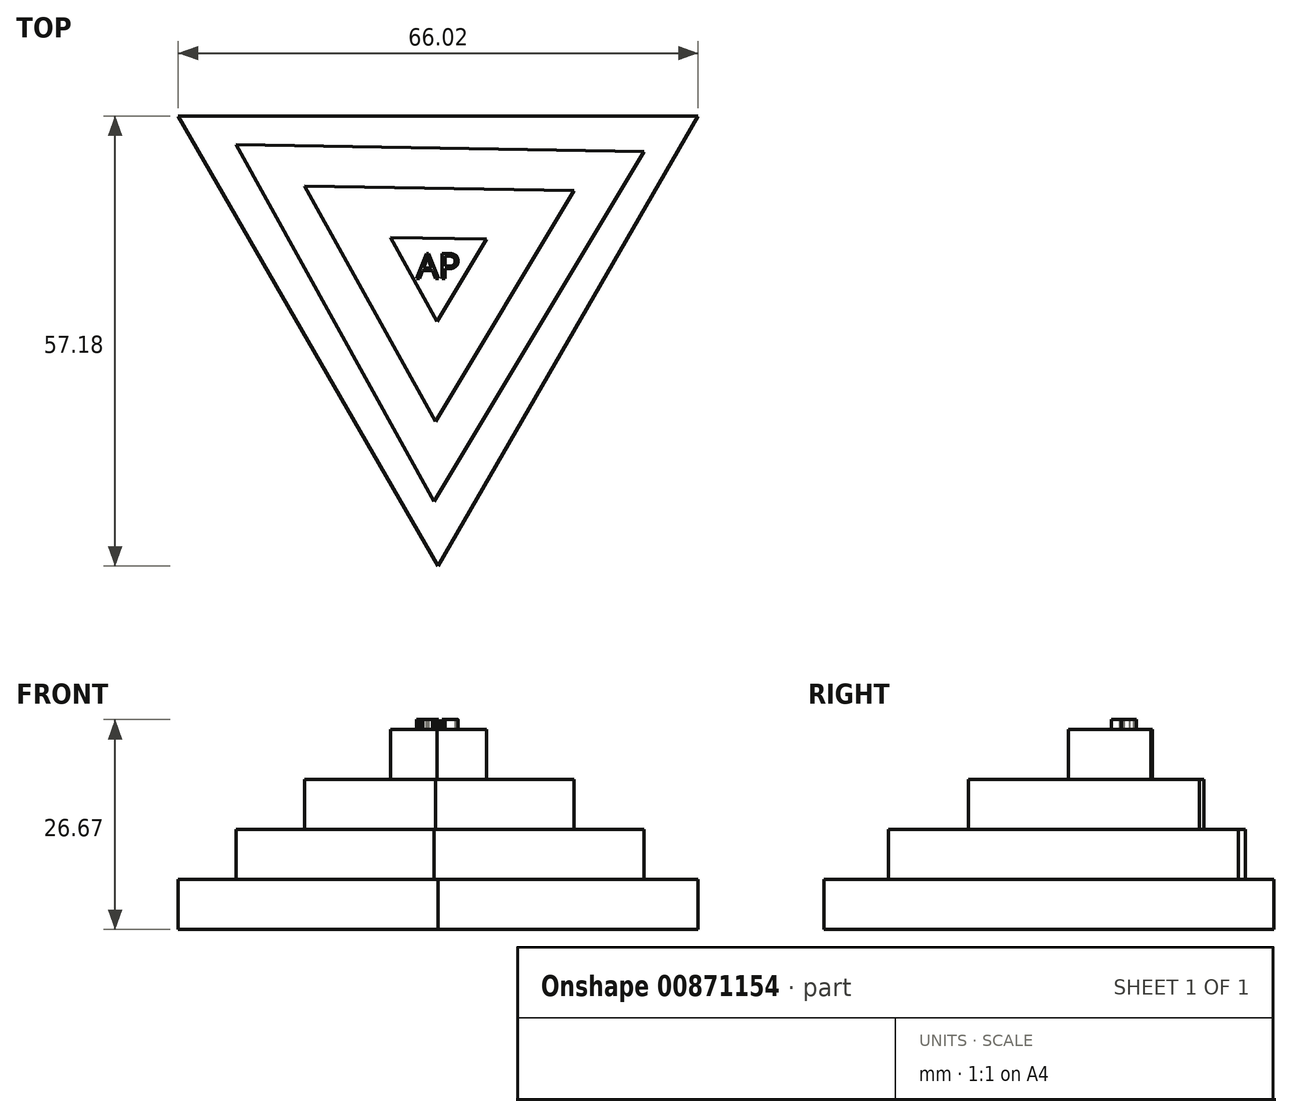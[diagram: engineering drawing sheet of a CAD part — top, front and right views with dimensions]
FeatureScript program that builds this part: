
annotation { "Feature Type Name" : "Feature", "Feature Type Description" : "" }
export const myFeature = defineFeature(function(context is Context, id is Id, definition is map)
    precondition{}
    {
        {
            var Q0;
            Q0=qCreatedBy(makeId("Top.planeOp"),FACE);
            var sketch = newSketch(context, id + "F0", { "sketchPlane" : qUnion([Q0])});
            skCircle(sketch, "E0.cCircle", {"center": v(0, 0) * mm, "radius": 19.06 * mm, "construction": true});
            skLineSegment(sketch, "E0.0", {"start": v(-33.01, 19.06) * mm, "end": v(33.01, 19.06) * mm});
            skLineSegment(sketch, "E0.1", {"start": v(33.01, 19.06) * mm, "end": v(0, -38.12) * mm});
            skLineSegment(sketch, "E0.2", {"start": v(0, -38.12) * mm, "end": v(-33.01, 19.06) * mm});
            skPoint(sketch, "E0.0.midPoint", {"position": v(0, 19.06) * mm});
            skPoint(sketch, "E1.startSnap0", {"position": v(-16.5, 9.53) * mm});
            skSolve(sketch);
        }
        {
            var Q0;
            Q0=makeQuery(id+"F0.imprint","IMPRINT",FACE,{"disambiguationData":[TD([[makeQuery(id+"F0.imprint","IMPRINT",EDGE,{"derivedFrom":sQuery(id+"F0.wireOp",EDGE,"E0.0")}),-1.0]])]});
            extrude(context, id + "F1", {"entities" : qUnion([Q0]), "depth" : 6.35 * mm, "offsetDistance" : 25.4 * mm});
        }
        {
            var Q0;
            Q0=makeQuery(id+"F1.opExtrude","CAP_FACE",FACE,{"disambiguationData":[OSD([sQuery(id+"F0.wireOp",EDGE,"E0.0"),sQuery(id+"F0.wireOp",EDGE,"E0.1"),sQuery(id+"F0.wireOp",EDGE,"E0.2")])],"isStart":false});
            var sketch = newSketch(context, id + "F2", { "sketchPlane" : qUnion([Q0])});
            skCircle(sketch, "E2.cCircle", {"center": v(0, 0) * mm, "radius": 14.95 * mm, "construction": true});
            skLineSegment(sketch, "E2.0", {"start": v(26.15, 14.5) * mm, "end": v(-0.51, -29.9) * mm});
            skLineSegment(sketch, "E2.1", {"start": v(-0.51, -29.9) * mm, "end": v(-25.64, 15.4) * mm});
            skLineSegment(sketch, "E2.2", {"start": v(-25.64, 15.4) * mm, "end": v(26.15, 14.5) * mm});
            skPoint(sketch, "E2.0.midPoint", {"position": v(12.82, -7.7) * mm});
            skSolve(sketch);
        }
        {
            var Q0;
            Q0 = qSketchRegion(id + "F2", true);
            extrude(context, id + "F3", {"entities" : qUnion([Q0]), "operationType" : NewBodyOperationType.ADD, "depth" : 6.35 * mm, "offsetDistance" : 25.4 * mm});
        }
        {
            var Q0;
            Q0=makeQuery(id+"F3.opExtrude","CAP_FACE",FACE,{"disambiguationData":[OSD([sQuery(id+"F2.wireOp",EDGE,"E2.0"),sQuery(id+"F2.wireOp",EDGE,"E2.1"),sQuery(id+"F2.wireOp",EDGE,"E2.2")])],"isStart":false});
            var sketch = newSketch(context, id + "F4", { "sketchPlane" : qUnion([Q0])});
            skLineSegment(sketch, "E3.0", {"start": v(17.27, 9.58) * mm, "end": v(-16.93, 10.17) * mm});
            skLineSegment(sketch, "E3.1", {"start": v(-0.34, -19.75) * mm, "end": v(17.27, 9.58) * mm});
            skLineSegment(sketch, "E3.2", {"start": v(-16.93, 10.17) * mm, "end": v(-0.34, -19.75) * mm});
            skSolve(sketch);
        }
        {
            var Q0;
            Q0 = qSketchRegion(id + "F4", true);
            extrude(context, id + "F5", {"entities" : qUnion([Q0]), "operationType" : NewBodyOperationType.ADD, "depth" : 6.35 * mm, "offsetDistance" : 25.4 * mm});
        }
        {
            var Q0;
            Q0=makeQuery(id+"F5.opExtrude","CAP_FACE",FACE,{"disambiguationData":[OSD([sQuery(id+"F4.wireOp",EDGE,"E3.0"),sQuery(id+"F4.wireOp",EDGE,"E3.1"),sQuery(id+"F4.wireOp",EDGE,"E3.2")])],"isStart":false});
            var sketch = newSketch(context, id + "F6", { "sketchPlane" : qUnion([Q0])});
            skLineSegment(sketch, "E4.0", {"start": v(6.16, 3.42) * mm, "end": v(-6.04, 3.63) * mm});
            skLineSegment(sketch, "E4.1", {"start": v(-0.12, -7.05) * mm, "end": v(6.16, 3.42) * mm});
            skLineSegment(sketch, "E4.2", {"start": v(-6.04, 3.63) * mm, "end": v(-0.12, -7.05) * mm});
            skSolve(sketch);
        }
        {
            var Q0;
            Q0 = qSketchRegion(id + "F6", true);
            extrude(context, id + "F7", {"entities" : qUnion([Q0]), "operationType" : NewBodyOperationType.ADD, "depth" : 6.35 * mm, "offsetDistance" : 25.4 * mm});
        }
        {
            var Q0;
            Q0=makeQuery(id+"F6.imprint","IMPRINT",FACE,{"disambiguationData":[TD([[makeQuery(id+"F6.imprint","IMPRINT",EDGE,{"derivedFrom":sQuery(id+"F6.wireOp",EDGE,"E4.0")}),-1.0]])]});
            var sketch = newSketch(context, id + "F8", { "sketchPlane" : qUnion([Q0])});
            skText(sketch, "E5", { "text": "AP", "fontName": "OpenSans-Regular.ttf"});
            const initialGuessF8  = {"E5": [-0.00275, -0.00161, 1, 0, 0.00322]};
            skSetInitialGuess(sketch, initialGuessF8);
            skSolve(sketch);
        }
        {
            var Q0;
            Q0 = qSketchRegion(id + "F8", true);
            extrude(context, id + "F9", {"entities" : qUnion([Q0]), "operationType" : NewBodyOperationType.ADD, "depth" : 7.62 * mm, "offsetDistance" : 25.4 * mm});
        }
    });
